# Revit family: Toilet-Intelligent-Floor_Mount-KOHLER-EIR-K-77795TW
name_source: partatom
category: Plumbing Fixtures
revit_build: Autodesk Revit 2017 (Build: 20160225_1515(x64)
units: mm (PartAtom-declared; Revit-internal decimal feet)

## family parameters
Cut with Voids When Loaded = No
Host = Face
OmniClass Number = 23.31.19.00
OmniClass Title = Toilets
Part Type = Normal
Room Calculation Point = No
Round Connector Dimension = Use Diameter
Shared = No

## types (2) — shared parameters
ADA Compliant = No
Apparent Load = 0 VA
Assembly Code = D2010100
CW Connection = Yes
Cold Water Inlet = Cold Water Inlet
Date Modified = 12/29/2020
Default Elevation = 0"
Description = Smart toilet
Electrical Connector = Yes
Electrical Note = One dedicated circuit required
Finish = Kohler-Vitreous_China-0-White
Flow Rate = 0 GPM
Flush Rate- GPF = 1.28 GPF
Flush Rate- LPF = 4.8 LPF
HW Connection = No
Height = 20 9/16"
Hot Water Inlet = Hot Water Inlet
Length = 27 9/16"
Manufacturer = KOHLER Co.
Master Format 2014 = 22 41 13.13
Master Format 2014 Name = Residential Water Closets
Material = Vitreous China
Pressure = 0.00 psi
Product Name = Eir
Product Page URL = https://www.kohler.com.tw
Rough-In = 12"
Seat Included = Yes
URL = https://www.kohlerasiapacific.com
Vent Connection = No
Voltage = 220 V
Waste Connection = Yes
Waste Water Outlet = Waste Water Outlet
WaterSense Certified = No
Width = 16 7/16"

## per-type parameters (varying)
| type | Model | Seat Rim Finish | Type |
| EX,0-White | K-77795TW-EX-0 | Kohler-Vitreous_China-0-White | 1 |
| EXSG,0-White | K-77795T-EXSG-0 | Kohler-Metal-PGD-Eternal_Gold | 2 |

## geometry (parser evidence)
native form markers: Sweep x6
no freeform markers — native parametric forms only
